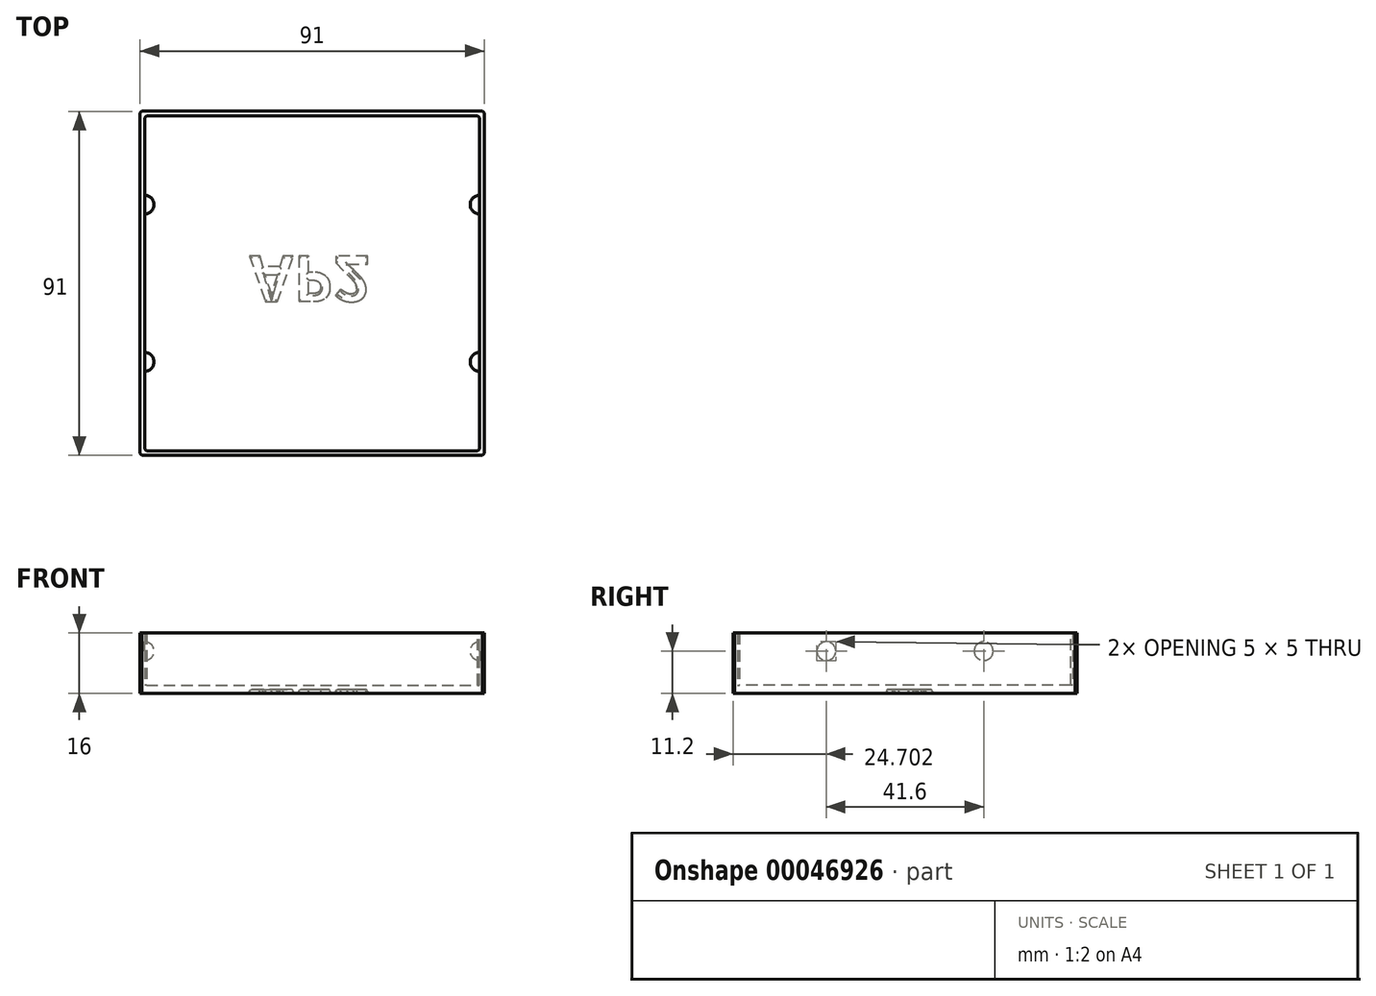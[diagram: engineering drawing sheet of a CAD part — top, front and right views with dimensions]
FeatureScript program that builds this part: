
annotation { "Feature Type Name" : "Feature", "Feature Type Description" : "" }
export const myFeature = defineFeature(function(context is Context, id is Id, definition is map)
    precondition{}
    {
        {
            var Q0;
            Q0=qCreatedBy(makeId("Top.planeOp"),FACE);
            var sketch = newSketch(context, id + "F0", { "sketchPlane" : qUnion([Q0])});
            skLineSegment(sketch, "E0.bottom", {"start": v(-34.06, 30.74) * mm, "end": v(56.94, 30.74) * mm});
            skLineSegment(sketch, "E0.top", {"start": v(-34.06, -60.26) * mm, "end": v(56.94, -60.26) * mm});
            skLineSegment(sketch, "E0.left", {"start": v(-34.06, 30.74) * mm, "end": v(-34.06, -60.26) * mm});
            skLineSegment(sketch, "E0.right", {"start": v(56.94, 30.74) * mm, "end": v(56.94, -60.26) * mm});
            skSolve(sketch);
        }
        {
            var Q0;
            Q0=qSketchRegion(id+"F0",true);
            extrude(context, id + "F1", {"entities" : qUnion([Q0]), "depth" : 15 * mm});
        }
        {
            var Q0;
            Q0=makeQuery(id+"F1.opExtrude","CAP_FACE",FACE,{"disambiguationData":[OSD([sQuery(id+"F0.wireOp",EDGE,"E0.bottom"),sQuery(id+"F0.wireOp",EDGE,"E0.top"),sQuery(id+"F0.wireOp",EDGE,"E0.left"),sQuery(id+"F0.wireOp",EDGE,"E0.right")])],"isStart":false});
            shell(context, id + "F2", {"entities" : qUnion([Q0]), "thickness" : 1.2 * mm});
        }
        {
            var Q0;
            Q0=makeQuery(id+"F1.opExtrude","SWEPT_EDGE",EDGE,{"disambiguationData":[OSD([sQuery(id+"F0.wireOp",EDGE,"E0.top"),sQuery(id+"F0.wireOp",EDGE,"E0.right")])]});
            chamfer(context, id + "F3", {"entities" : qUnion([Q0]), "width" : 0.5 * mm, "tangentPropagation" : true});
        }
        {
            var Q0;
            Q0=makeQuery(id+"F1.opExtrude","SWEPT_EDGE",EDGE,{"disambiguationData":[OSD([sQuery(id+"F0.wireOp",EDGE,"E0.top"),sQuery(id+"F0.wireOp",EDGE,"E0.left")])]});
            chamfer(context, id + "F4", {"entities" : qUnion([Q0]), "width" : 0.5 * mm, "tangentPropagation" : true});
        }
        {
            var Q0;
            Q0=makeQuery(id+"F1.opExtrude","SWEPT_EDGE",EDGE,{"disambiguationData":[OSD([sQuery(id+"F0.wireOp",EDGE,"E0.bottom"),sQuery(id+"F0.wireOp",EDGE,"E0.left")])]});
            chamfer(context, id + "F5", {"entities" : qUnion([Q0]), "width" : 0.5 * mm, "tangentPropagation" : true});
        }
        {
            var Q0;
            Q0=makeQuery(id+"F1.opExtrude","SWEPT_EDGE",EDGE,{"disambiguationData":[OSD([sQuery(id+"F0.wireOp",EDGE,"E0.bottom"),sQuery(id+"F0.wireOp",EDGE,"E0.right")])]});
            chamfer(context, id + "F6", {"entities" : qUnion([Q0]), "width" : 0.5 * mm, "tangentPropagation" : true});
        }
        {
            var Q0;
            Q0=makeQuery(id+"F2.opShell","OFFSET_EDGE",EDGE,{"disambiguationData":[OSD([sQuery(id+"F0.wireOp",EDGE,"E0.bottom"),sQuery(id+"F0.wireOp",EDGE,"E0.right")])]});
            chamfer(context, id + "F7", {"entities" : qUnion([Q0]), "width" : 0.5 * mm, "tangentPropagation" : true});
        }
        {
            var Q0;
            Q0=makeQuery(id+"F2.opShell","OFFSET_EDGE",EDGE,{"disambiguationData":[OSD([sQuery(id+"F0.wireOp",EDGE,"E0.bottom"),sQuery(id+"F0.wireOp",EDGE,"E0.left")])]});
            chamfer(context, id + "F8", {"entities" : qUnion([Q0]), "width" : 0.5 * mm, "tangentPropagation" : true});
        }
        {
            var Q0;
            Q0=makeQuery(id+"F2.opShell","OFFSET_EDGE",EDGE,{"disambiguationData":[OSD([sQuery(id+"F0.wireOp",EDGE,"E0.top"),sQuery(id+"F0.wireOp",EDGE,"E0.right")])]});
            var Q1;
            Q1=makeQuery(id+"F2.opShell","OFFSET_EDGE",EDGE,{"disambiguationData":[OSD([sQuery(id+"F0.wireOp",EDGE,"E0.top"),sQuery(id+"F0.wireOp",EDGE,"E0.left")])]});
            chamfer(context, id + "F9", {"entities" : qUnion([Q0, Q1]), "width" : 0.5 * mm, "tangentPropagation" : true});
        }
        {
            var Q0;
            Q0=makeQuery(id+"Flp0mdXWCtvHWMH_1.boolean.opBoolean","MERGE",FACE,{"derivedFrom":[makeQuery(id+"F2.opShell","OFFSET_FACE",FACE,{"disambiguationData":[OSD([sQuery(id+"F0.wireOp",EDGE,"E0.left")])]}),makeQuery(id+"Flp0mdXWCtvHWMH_1.opExtrude","CAP_FACE",FACE,{"disambiguationData":[OSD([sQuery(id+"FTPc9KxoIFbVXmh_1.wireOp",EDGE,"aef7374d-b786-4aa7-95e7-22ee6e6e7421"),sQuery(id+"FTPc9KxoIFbVXmh_1.wireOp",EDGE,"174458bd-a122-4da6-bab4-8f87da723df8"),sQuery(id+"FTPc9KxoIFbVXmh_1.wireOp",EDGE,"06070032-cd5d-48af-bd01-3e7dc4a77fa4"),sQuery(id+"FTPc9KxoIFbVXmh_1.wireOp",EDGE,"0eff3254-9ddc-497c-9197-32e9d3974209")])],"isStart":false})]});
            var sketch = newSketch(context, id + "F10", { "sketchPlane" : qUnion([Q0])});
            skPoint(sketch, "E1", {"position": v(-35.56, 10.2) * mm});
            skCircle(sketch, "E2", {"center": v(-35.56, 10.2) * mm, "radius": 2.5 * mm});
            skLineSegment(sketch, "E3", {"start": v(-35.56, 10.2) * mm, "end": v(-33.06, 10.2) * mm});
            skLineSegment(sketch, "E4", {"start": v(-35.56, 10.2) * mm, "end": v(-38.06, 10.2) * mm});
            skPoint(sketch, "E5", {"position": v(6.04, 10.2) * mm});
            skCircle(sketch, "E6", {"center": v(6.04, 10.2) * mm, "radius": 2.5 * mm});
            skLineSegment(sketch, "E7", {"start": v(6.04, 10.2) * mm, "end": v(8.54, 10.2) * mm});
            skLineSegment(sketch, "E8", {"start": v(6.04, 10.2) * mm, "end": v(3.54, 10.2) * mm});
            skSolve(sketch);
        }
        {
            var Q0;
            {var subQ1=sQuery(id+"F10.wireOp",EDGE,"E3");Q0=makeQuery(id+"F10.imprint","IMPRINT",FACE,{"disambiguationData":[TD([[makeQuery(id+"F10.imprint","IMPRINT",EDGE,{"derivedFrom":subQ1}),1.0]])]});}
            var Q1;
            Q1=sQuery(id+"F10.wireOp",EDGE,"E3");
            revolve(context, id + "F11", {"operationType" : NewBodyOperationType.ADD, "entities" : qUnion([Q0]), "axis" : qUnion([Q1]), "revolveType" : RevolveType.ONE_DIRECTION, "angle" : 180 * degree});
        }
        {
            var Q0;
            {var subQ1=sQuery(id+"F10.wireOp",EDGE,"E7");Q0=makeQuery(id+"F10.imprint","IMPRINT",FACE,{"disambiguationData":[TD([[makeQuery(id+"F10.imprint","IMPRINT",EDGE,{"derivedFrom":subQ1}),1.0]])]});}
            var Q1;
            Q1=sQuery(id+"F10.wireOp",EDGE,"E7");
            revolve(context, id + "F12", {"operationType" : NewBodyOperationType.ADD, "entities" : qUnion([Q0]), "axis" : qUnion([Q1]), "revolveType" : RevolveType.ONE_DIRECTION, "angle" : 180 * degree});
        }
        {
            var Q0;
            Q0=makeQuery(id+"FwOUtTcqqzjjj6q_1.boolean.opBoolean","MERGE",FACE,{"derivedFrom":[makeQuery(id+"F2.opShell","OFFSET_FACE",FACE,{"disambiguationData":[OSD([sQuery(id+"F0.wireOp",EDGE,"E0.right")])]}),makeQuery(id+"FwOUtTcqqzjjj6q_1.opExtrude","CAP_FACE",FACE,{"disambiguationData":[OSD([sQuery(id+"FWyYdWf3gWrX6na_1.wireOp",EDGE,"ca5ce68c-f7c0-4bf3-b04c-01e4b41dda39.bottom"),sQuery(id+"FWyYdWf3gWrX6na_1.wireOp",EDGE,"ca5ce68c-f7c0-4bf3-b04c-01e4b41dda39.top"),sQuery(id+"FWyYdWf3gWrX6na_1.wireOp",EDGE,"05e8e774-b76b-422d-b93c-fcf6dea86ba3"),sQuery(id+"FWyYdWf3gWrX6na_1.wireOp",EDGE,"3b75f1f9-5f48-4d32-981a-030c2a5a454a")])],"isStart":false})]});
            var sketch = newSketch(context, id + "F13", { "sketchPlane" : qUnion([Q0])});
            skPoint(sketch, "E9", {"position": v(-6.04, 10.2) * mm});
            skPoint(sketch, "E10", {"position": v(35.56, 10.2) * mm});
            skCircle(sketch, "E11", {"center": v(-6.04, 10.2) * mm, "radius": 2.5 * mm});
            skCircle(sketch, "E12", {"center": v(35.56, 10.2) * mm, "radius": 2.5 * mm});
            skLineSegment(sketch, "E13", {"start": v(-6.04, 10.2) * mm, "end": v(-8.54, 10.2) * mm});
            skLineSegment(sketch, "E14", {"start": v(-6.04, 10.2) * mm, "end": v(-3.54, 10.2) * mm});
            skLineSegment(sketch, "E15", {"start": v(35.56, 10.2) * mm, "end": v(38.06, 10.2) * mm});
            skLineSegment(sketch, "E16", {"start": v(35.56, 10.2) * mm, "end": v(33.06, 10.2) * mm});
            skSolve(sketch);
        }
        {
            var Q0;
            {var subQ0=sQuery(id+"F13.wireOp",EDGE,"E13");Q0=makeQuery(id+"F13.imprint","IMPRINT",FACE,{"disambiguationData":[TD([[makeQuery(id+"F13.imprint","IMPRINT",EDGE,{"derivedFrom":subQ0}),-1.0]])]});}
            var Q1;
            Q1=sQuery(id+"F13.wireOp",EDGE,"E14");
            revolve(context, id + "F14", {"operationType" : NewBodyOperationType.ADD, "entities" : qUnion([Q0]), "axis" : qUnion([Q1]), "revolveType" : RevolveType.ONE_DIRECTION, "angle" : 180 * degree});
        }
        {
            var Q0;
            {var subQ0=sQuery(id+"F13.wireOp",EDGE,"E15");Q0=makeQuery(id+"F13.imprint","IMPRINT",FACE,{"disambiguationData":[TD([[makeQuery(id+"F13.imprint","IMPRINT",EDGE,{"derivedFrom":subQ0}),1.0]])]});}
            var Q1;
            Q1=sQuery(id+"F13.wireOp",EDGE,"E15");
            revolve(context, id + "F15", {"operationType" : NewBodyOperationType.ADD, "entities" : qUnion([Q0]), "axis" : qUnion([Q1]), "revolveType" : RevolveType.ONE_DIRECTION, "angle" : 180 * degree});
        }
        {
            var Q0;
            Q0=makeQuery(id+"F1.opExtrude","CAP_FACE",FACE,{"disambiguationData":[OSD([sQuery(id+"F0.wireOp",EDGE,"E0.bottom"),sQuery(id+"F0.wireOp",EDGE,"E0.top"),sQuery(id+"F0.wireOp",EDGE,"E0.left"),sQuery(id+"F0.wireOp",EDGE,"E0.right")])],"isStart":true});
            extrude(context, id + "F16", {"entities" : qUnion([Q0]), "operationType" : NewBodyOperationType.ADD, "depth" : 1 * mm});
        }
        {
            var Q0;
            Q0=makeQuery(id+"F16.opExtrude","CAP_FACE",FACE,{"disambiguationData":[OSD([sQuery(id+"F0.wireOp",EDGE,"E0.bottom"),sQuery(id+"F0.wireOp",EDGE,"E0.top"),sQuery(id+"F0.wireOp",EDGE,"E0.left"),sQuery(id+"F0.wireOp",EDGE,"E0.right")])],"isStart":false});
            var sketch = newSketch(context, id + "F17", { "sketchPlane" : qUnion([Q0])});
            skText(sketch, "E17", { "text": "AP2", "fontName": "OpenSans-Bold.ttf"});
            const initialGuessF17  = {"E17": [-0.00514, 0.00755, 1, 0, 0.0121]};
            skSetInitialGuess(sketch, initialGuessF17);
            skSolve(sketch);
        }
        {
            var Q0;
            Q0 = qSketchRegion(id + "F17", true);
            extrude(context, id + "F18", {"entities" : qUnion([Q0]), "operationType" : NewBodyOperationType.REMOVE, "oppositeDirection" : true, "depth" : 1 * mm});
        }
        {
            var Q0;
            Q0=makeQuery(id+"F18.boolean.opBoolean","COPY",FACE,{"derivedFrom":makeQuery(id+"F18.opExtrude","CAP_FACE",FACE,{"disambiguationData":[OSD([sQuery(id+"F17.wireOp",EDGE,"E17.sketch_text.stroke-0"),sQuery(id+"F17.wireOp",EDGE,"E17.sketch_text.stroke-1"),sQuery(id+"F17.wireOp",EDGE,"E17.sketch_text.stroke-2"),sQuery(id+"F17.wireOp",EDGE,"E17.sketch_text.stroke-3"),sQuery(id+"F17.wireOp",EDGE,"E17.sketch_text.stroke-4"),sQuery(id+"F17.wireOp",EDGE,"E17.sketch_text.stroke-5"),sQuery(id+"F17.wireOp",EDGE,"E17.sketch_text.stroke-6"),sQuery(id+"F17.wireOp",EDGE,"E17.sketch_text.stroke-7"),sQuery(id+"F17.wireOp",EDGE,"E17.sketch_text.stroke-8"),sQuery(id+"F17.wireOp",EDGE,"E17.sketch_text.stroke-9"),sQuery(id+"F17.wireOp",EDGE,"E17.sketch_text.stroke-10"),sQuery(id+"F17.wireOp",EDGE,"E17.sketch_text.stroke-11")])],"isStart":false})});
            var Q1;
            Q1=makeQuery(id+"F18.boolean.opBoolean","COPY",FACE,{"derivedFrom":makeQuery(id+"F18.opExtrude","CAP_FACE",FACE,{"disambiguationData":[OSD([sQuery(id+"F17.wireOp",EDGE,"E17.sketch_text.stroke-12"),sQuery(id+"F17.wireOp",EDGE,"E17.sketch_text.stroke-13"),sQuery(id+"F17.wireOp",EDGE,"E17.sketch_text.stroke-14"),sQuery(id+"F17.wireOp",EDGE,"E17.sketch_text.stroke-15"),sQuery(id+"F17.wireOp",EDGE,"E17.sketch_text.stroke-16"),sQuery(id+"F17.wireOp",EDGE,"E17.sketch_text.stroke-17"),sQuery(id+"F17.wireOp",EDGE,"E17.sketch_text.stroke-18"),sQuery(id+"F17.wireOp",EDGE,"E17.sketch_text.stroke-19"),sQuery(id+"F17.wireOp",EDGE,"E17.sketch_text.stroke-20"),sQuery(id+"F17.wireOp",EDGE,"E17.sketch_text.stroke-21"),sQuery(id+"F17.wireOp",EDGE,"E17.sketch_text.stroke-22"),sQuery(id+"F17.wireOp",EDGE,"E17.sketch_text.stroke-23"),sQuery(id+"F17.wireOp",EDGE,"E17.sketch_text.stroke-24"),sQuery(id+"F17.wireOp",EDGE,"E17.sketch_text.stroke-25"),sQuery(id+"F17.wireOp",EDGE,"E17.sketch_text.stroke-26"),sQuery(id+"F17.wireOp",EDGE,"E17.sketch_text.stroke-27")])],"isStart":false})});
            var Q2;
            Q2=makeQuery(id+"F18.boolean.opBoolean","COPY",FACE,{"derivedFrom":makeQuery(id+"F18.opExtrude","CAP_FACE",FACE,{"disambiguationData":[OSD([sQuery(id+"F17.wireOp",EDGE,"E17.sketch_text.stroke-28"),sQuery(id+"F17.wireOp",EDGE,"E17.sketch_text.stroke-29"),sQuery(id+"F17.wireOp",EDGE,"E17.sketch_text.stroke-30"),sQuery(id+"F17.wireOp",EDGE,"E17.sketch_text.stroke-31"),sQuery(id+"F17.wireOp",EDGE,"E17.sketch_text.stroke-32"),sQuery(id+"F17.wireOp",EDGE,"E17.sketch_text.stroke-33"),sQuery(id+"F17.wireOp",EDGE,"E17.sketch_text.stroke-34"),sQuery(id+"F17.wireOp",EDGE,"E17.sketch_text.stroke-35"),sQuery(id+"F17.wireOp",EDGE,"E17.sketch_text.stroke-36"),sQuery(id+"F17.wireOp",EDGE,"E17.sketch_text.stroke-37"),sQuery(id+"F17.wireOp",EDGE,"E17.sketch_text.stroke-38"),sQuery(id+"F17.wireOp",EDGE,"E17.sketch_text.stroke-39"),sQuery(id+"F17.wireOp",EDGE,"E17.sketch_text.stroke-40"),sQuery(id+"F17.wireOp",EDGE,"E17.sketch_text.stroke-41"),sQuery(id+"F17.wireOp",EDGE,"E17.sketch_text.stroke-42"),sQuery(id+"F17.wireOp",EDGE,"E17.sketch_text.stroke-43"),sQuery(id+"F17.wireOp",EDGE,"E17.sketch_text.stroke-44"),sQuery(id+"F17.wireOp",EDGE,"E17.sketch_text.stroke-45"),sQuery(id+"F17.wireOp",EDGE,"E17.sketch_text.stroke-46"),sQuery(id+"F17.wireOp",EDGE,"E17.sketch_text.stroke-47"),sQuery(id+"F17.wireOp",EDGE,"E17.sketch_text.stroke-48"),sQuery(id+"F17.wireOp",EDGE,"E17.sketch_text.stroke-49"),sQuery(id+"F17.wireOp",EDGE,"E17.sketch_text.stroke-50"),sQuery(id+"F17.wireOp",EDGE,"E17.sketch_text.stroke-51")])],"isStart":false})});
            fillet(context, id + "F19", {"entities" : qUnion([Q0, Q1, Q2]), "radius" : 0.5 * mm, "tangentPropagation" : true, "allowEdgeOverflow" : false});
        }
    });
